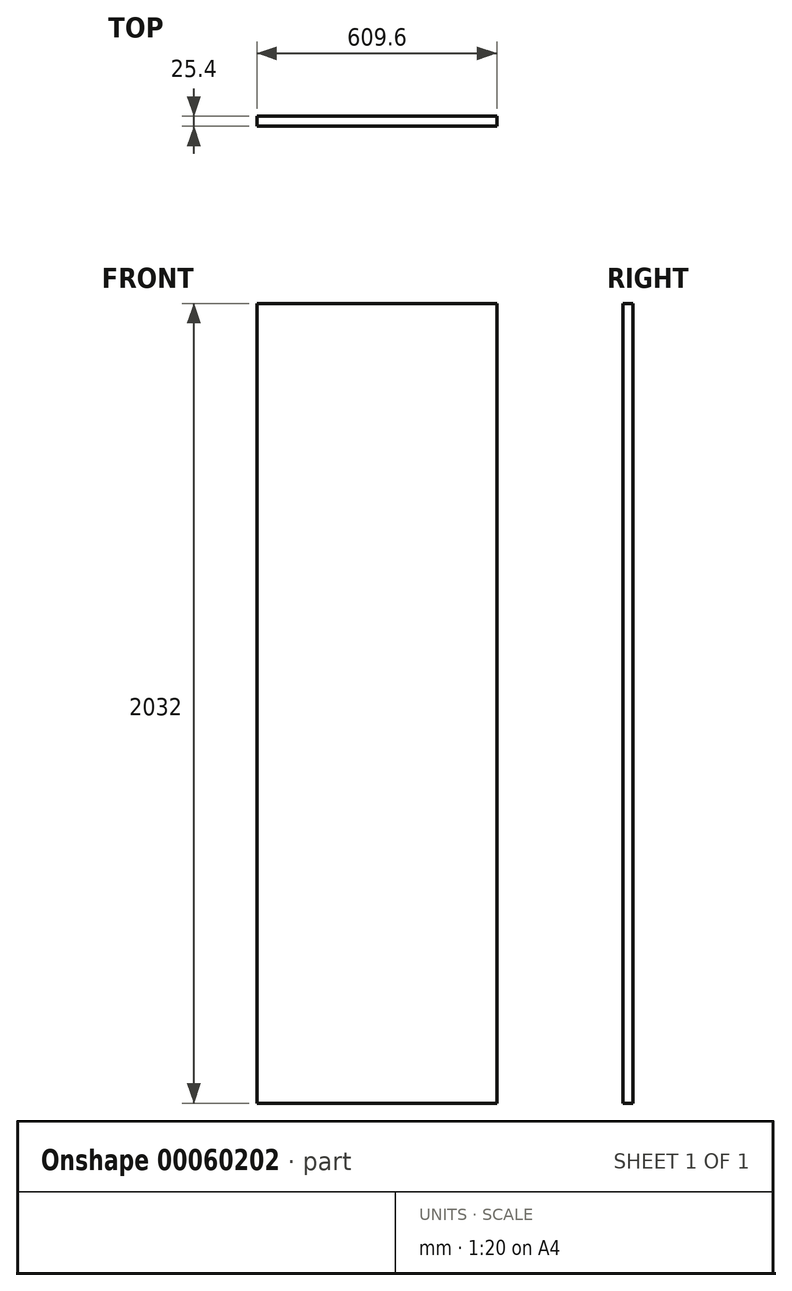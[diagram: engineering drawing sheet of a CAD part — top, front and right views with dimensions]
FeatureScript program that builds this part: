
annotation { "Feature Type Name" : "Feature", "Feature Type Description" : "" }
export const myFeature = defineFeature(function(context is Context, id is Id, definition is map)
    precondition{}
    {
        {
            var Q0;
            Q0=qCreatedBy(makeId("Front.planeOp"),FACE);
            var sketch = newSketch(context, id + "F0", { "sketchPlane" : qUnion([Q0])});
            skLineSegment(sketch, "E0.bottom", {"start": v(-340.68, 1280.87) * mm, "end": v(268.92, 1280.87) * mm});
            skLineSegment(sketch, "E0.top", {"start": v(-340.68, -751.13) * mm, "end": v(268.92, -751.13) * mm});
            skLineSegment(sketch, "E0.left", {"start": v(-340.68, 1280.87) * mm, "end": v(-340.68, -751.13) * mm});
            skLineSegment(sketch, "E0.right", {"start": v(268.92, 1280.87) * mm, "end": v(268.92, -751.13) * mm});
            skSolve(sketch);
        }
        {
            var Q0;
            Q0=makeQuery(id+"F0.imprint","IMPRINT",FACE,{"disambiguationData":[TD([[makeQuery(id+"F0.imprint","IMPRINT",EDGE,{"derivedFrom":sQuery(id+"F0.wireOp",EDGE,"E0.bottom")}),-1.0]])]});
            extrude(context, id + "F1", {"entities" : qUnion([Q0]), "depth" : 25.4 * mm});
        }
    });
